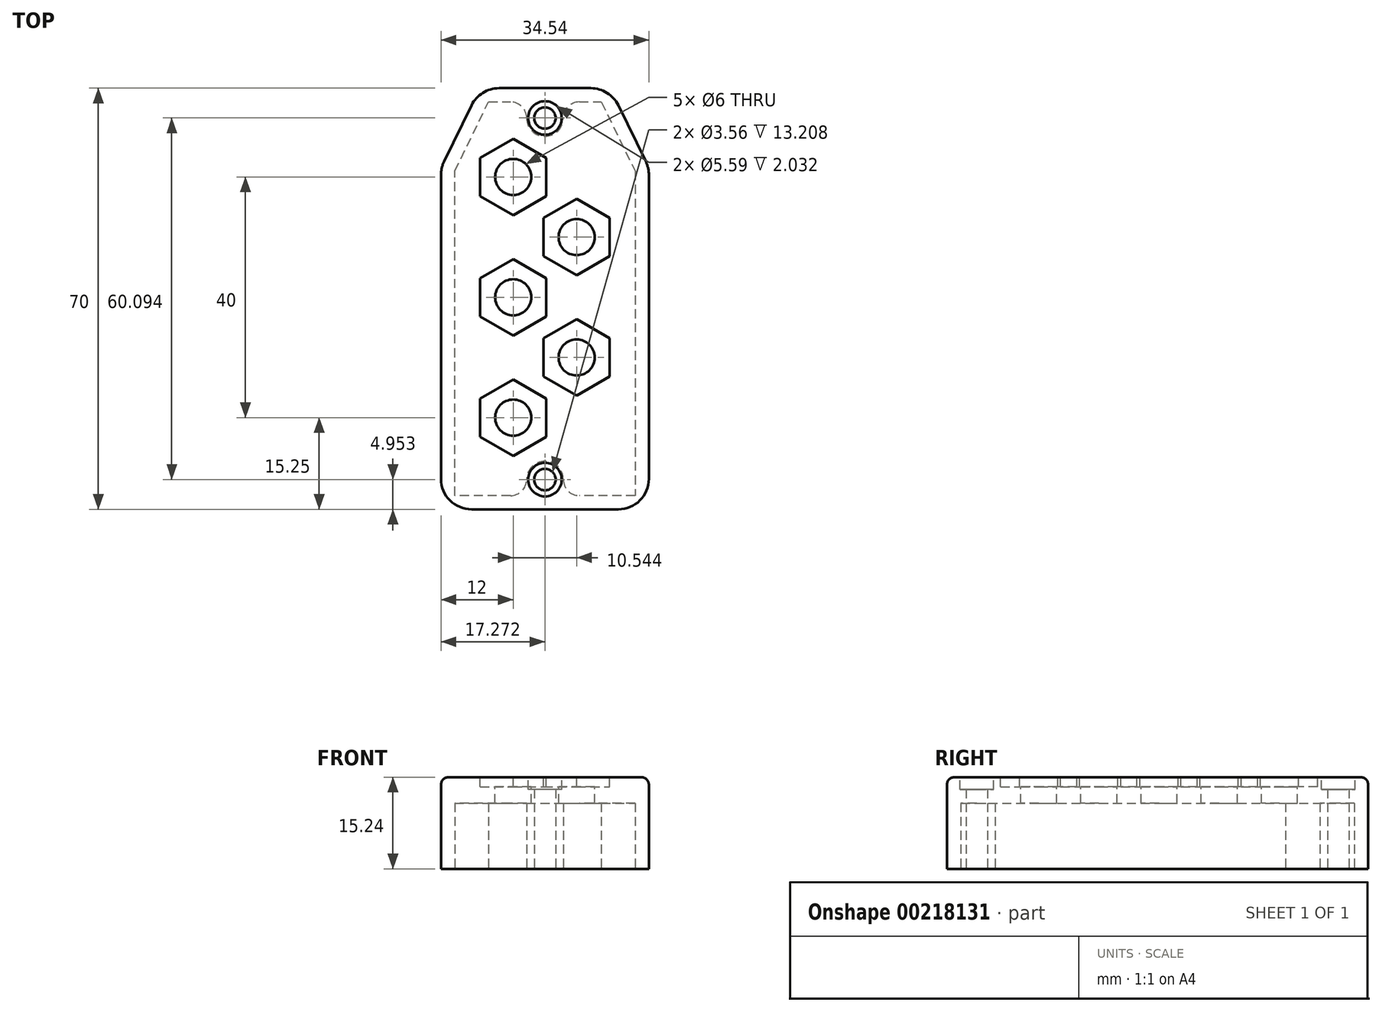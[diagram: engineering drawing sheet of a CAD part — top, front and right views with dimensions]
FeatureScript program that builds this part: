
annotation { "Feature Type Name" : "Feature", "Feature Type Description" : "" }
export const myFeature = defineFeature(function(context is Context, id is Id, definition is map)
    precondition{}
    {
        {
            var Q0;
            Q0=qCreatedBy(makeId("Top.planeOp"),FACE);
            var sketch = newSketch(context, id + "F0", { "sketchPlane" : qUnion([Q0])});
            skLineSegment(sketch, "E0", {"start": v(0, 0) * mm, "end": v(0, 56.78) * mm});
            skLineSegment(sketch, "E1", {"start": v(0, 56.78) * mm, "end": v(6.48, 70) * mm});
            skLineSegment(sketch, "E2", {"start": v(6.48, 70) * mm, "end": v(28.07, 70) * mm});
            skLineSegment(sketch, "E3", {"start": v(28.07, 70) * mm, "end": v(34.54, 56.78) * mm});
            skLineSegment(sketch, "E4", {"start": v(34.54, 56.78) * mm, "end": v(34.54, 0) * mm});
            skLineSegment(sketch, "E5", {"start": v(34.54, 0) * mm, "end": v(0, 0) * mm});
            skLineSegment(sketch, "E6", {"start": v(17.27, 70) * mm, "end": v(17.27, 0) * mm, "construction": true});
            skCircle(sketch, "E7", {"center": v(17.27, 65.05) * mm, "radius": 1.78 * mm});
            skCircle(sketch, "E8", {"center": v(17.27, 4.95) * mm, "radius": 1.78 * mm});
            skSolve(sketch);
        }
        {
            var Q0;
            Q0=makeQuery(id+"F0.imprint","IMPRINT",FACE,{"disambiguationData":[TD([[makeQuery(id+"F0.imprint","IMPRINT",EDGE,{"derivedFrom":sQuery(id+"F0.wireOp",EDGE,"E0")}),-1.0]])]});
            extrude(context, id + "F1", {"entities" : qUnion([Q0]), "depth" : 15.24 * mm});
        }
        {
            var Q0;
            Q0=makeQuery(id+"F1.opExtrude","CAP_FACE",FACE,{"disambiguationData":[OSD([sQuery(id+"F0.wireOp",EDGE,"E0"),sQuery(id+"F0.wireOp",EDGE,"E1"),sQuery(id+"F0.wireOp",EDGE,"E2"),sQuery(id+"F0.wireOp",EDGE,"E3"),sQuery(id+"F0.wireOp",EDGE,"E4"),sQuery(id+"F0.wireOp",EDGE,"E5"),sQuery(id+"F0.wireOp",EDGE,"E7"),sQuery(id+"F0.wireOp",EDGE,"E8")])],"isStart":true});
            var sketch = newSketch(context, id + "F2", { "sketchPlane" : qUnion([Q0])});
            skLineSegment(sketch, "E9.0", {"start": v(32.26, -56.25) * mm, "end": v(32.26, -2.29) * mm});
            skLineSegment(sketch, "E9.1", {"start": v(2.29, -2.29) * mm, "end": v(2.29, -56.25) * mm});
            skLineSegment(sketch, "E9.2", {"start": v(2.29, -56.25) * mm, "end": v(7.9, -67.71) * mm});
            skLineSegment(sketch, "E9.3", {"start": v(32.26, -2.29) * mm, "end": v(22.99, -2.29) * mm});
            skLineSegment(sketch, "E9.4", {"start": v(7.9, -67.71) * mm, "end": v(11.56, -67.71) * mm});
            skLineSegment(sketch, "E9.5", {"start": v(26.64, -67.71) * mm, "end": v(32.26, -56.25) * mm});
            skArc(sketch, "E10.0", {"start": v(14.22, -4.95) * mm, "mid": v(17.27, -8) * mm, "end": v(20.32, -4.95) * mm});
            skArc(sketch, "E11.0", {"start": v(20.32, -65.05) * mm, "mid": v(17.27, -62) * mm, "end": v(14.22, -65.05) * mm});
            skArc(sketch, "E12", {"start": v(14.22, -4.95) * mm, "mid": v(13.44, -3.07) * mm, "end": v(11.56, -2.29) * mm});
            skArc(sketch, "E13", {"start": v(22.99, -2.29) * mm, "mid": v(21.1, -3.07) * mm, "end": v(20.32, -4.95) * mm});
            skArc(sketch, "E14", {"start": v(20.32, -65.05) * mm, "mid": v(21.1, -66.93) * mm, "end": v(22.99, -67.71) * mm});
            skArc(sketch, "E15", {"start": v(11.56, -67.71) * mm, "mid": v(13.44, -66.93) * mm, "end": v(14.22, -65.05) * mm});
            skLineSegment(sketch, "E16.trimOffspring", {"start": v(11.56, -2.29) * mm, "end": v(2.29, -2.29) * mm});
            skPoint(sketch, "E17.start.orphan", {"position": v(14.22, -2.29) * mm});
            skPoint(sketch, "E18.trimOffspring.start.orphan", {"position": v(20.32, -2.29) * mm});
            skLineSegment(sketch, "E19.trimOffspring", {"start": v(22.99, -67.71) * mm, "end": v(26.64, -67.71) * mm});
            skPoint(sketch, "E20.orphan", {"position": v(14.22, -67.71) * mm});
            skPoint(sketch, "E21.orphan", {"position": v(18.75, -67.71) * mm});
            skPoint(sketch, "E22.start.orphan", {"position": v(20.32, -67.71) * mm});
            skSolve(sketch);
        }
        {
            var Q0;
            Q0 = qSketchRegion(id + "F2", true);
            extrude(context, id + "F3", {"entities" : qUnion([Q0]), "operationType" : NewBodyOperationType.REMOVE, "oppositeDirection" : true, "depth" : 10.92 * mm});
        }
        {
            var Q0;
            Q0=makeQuery(id+"F1.opExtrude","SWEPT_EDGE",EDGE,{"disambiguationData":[OSD([sQuery(id+"F0.wireOp",EDGE,"E1"),sQuery(id+"F0.wireOp",EDGE,"E2")])]});
            var Q1;
            Q1=makeQuery(id+"F1.opExtrude","SWEPT_EDGE",EDGE,{"disambiguationData":[OSD([sQuery(id+"F0.wireOp",EDGE,"E2"),sQuery(id+"F0.wireOp",EDGE,"E3")])]});
            var Q2;
            Q2=makeQuery(id+"F1.opExtrude","SWEPT_EDGE",EDGE,{"disambiguationData":[OSD([sQuery(id+"F0.wireOp",EDGE,"E3"),sQuery(id+"F0.wireOp",EDGE,"E4")])]});
            var Q3;
            Q3=makeQuery(id+"F1.opExtrude","SWEPT_EDGE",EDGE,{"disambiguationData":[OSD([sQuery(id+"F0.wireOp",EDGE,"E4"),sQuery(id+"F0.wireOp",EDGE,"E5")])]});
            var Q4;
            Q4=makeQuery(id+"F1.opExtrude","SWEPT_EDGE",EDGE,{"disambiguationData":[OSD([sQuery(id+"F0.wireOp",EDGE,"E0"),sQuery(id+"F0.wireOp",EDGE,"E5")])]});
            var Q5;
            Q5=makeQuery(id+"F1.opExtrude","SWEPT_EDGE",EDGE,{"disambiguationData":[OSD([sQuery(id+"F0.wireOp",EDGE,"E0"),sQuery(id+"F0.wireOp",EDGE,"E1")])]});
            fillet(context, id + "F4", {"entities" : qUnion([Q0, Q1, Q2, Q3, Q4, Q5]), "radius" : 5.08 * mm, "tangentPropagation" : true, "allowEdgeOverflow" : false});
        }
        {
            var Q0;
            {var subQ0=sQuery(id+"F0.wireOp",EDGE,"E5");var subQ1=sQuery(id+"F0.wireOp",EDGE,"E0");Q0=makeQuery(id+"F4.opFillet","BLEND_EDGE",EDGE,{"blendedFrom":[makeQuery(id+"F1.opExtrude","SWEPT_EDGE",EDGE,{"disambiguationData":[OSD([subQ1,subQ0])]}),makeQuery(id+"F1.opExtrude","CAP_FACE",FACE,{"disambiguationData":[OSD([subQ1,sQuery(id+"F0.wireOp",EDGE,"E1"),sQuery(id+"F0.wireOp",EDGE,"E2"),sQuery(id+"F0.wireOp",EDGE,"E3"),sQuery(id+"F0.wireOp",EDGE,"E4"),subQ0,sQuery(id+"F0.wireOp",EDGE,"E7"),sQuery(id+"F0.wireOp",EDGE,"E8")])],"isStart":false})],"blendedInto":[makeQuery(id+"F1.opExtrude","CAP_FACE",FACE,{"disambiguationData":[OSD([subQ1,sQuery(id+"F0.wireOp",EDGE,"E1"),sQuery(id+"F0.wireOp",EDGE,"E2"),sQuery(id+"F0.wireOp",EDGE,"E3"),sQuery(id+"F0.wireOp",EDGE,"E4"),subQ0,sQuery(id+"F0.wireOp",EDGE,"E7"),sQuery(id+"F0.wireOp",EDGE,"E8")])],"isStart":false})]});}
            var Q1;
            {var subQ0=sQuery(id+"F0.wireOp",EDGE,"E5");var subQ1=sQuery(id+"F0.wireOp",EDGE,"E4");Q1=makeQuery(id+"F4.opFillet","BLEND_EDGE",EDGE,{"blendedFrom":[makeQuery(id+"F1.opExtrude","SWEPT_EDGE",EDGE,{"disambiguationData":[OSD([subQ1,subQ0])]}),makeQuery(id+"F1.opExtrude","CAP_FACE",FACE,{"disambiguationData":[OSD([sQuery(id+"F0.wireOp",EDGE,"E0"),sQuery(id+"F0.wireOp",EDGE,"E1"),sQuery(id+"F0.wireOp",EDGE,"E2"),sQuery(id+"F0.wireOp",EDGE,"E3"),subQ1,subQ0,sQuery(id+"F0.wireOp",EDGE,"E7"),sQuery(id+"F0.wireOp",EDGE,"E8")])],"isStart":false})],"blendedInto":[makeQuery(id+"F1.opExtrude","CAP_FACE",FACE,{"disambiguationData":[OSD([sQuery(id+"F0.wireOp",EDGE,"E0"),sQuery(id+"F0.wireOp",EDGE,"E1"),sQuery(id+"F0.wireOp",EDGE,"E2"),sQuery(id+"F0.wireOp",EDGE,"E3"),subQ1,subQ0,sQuery(id+"F0.wireOp",EDGE,"E7"),sQuery(id+"F0.wireOp",EDGE,"E8")])],"isStart":false})]});}
            var Q2;
            {var subQ0=sQuery(id+"F0.wireOp",EDGE,"E4");var subQ1=sQuery(id+"F0.wireOp",EDGE,"E3");Q2=makeQuery(id+"F4.opFillet","BLEND_EDGE",EDGE,{"blendedFrom":[makeQuery(id+"F1.opExtrude","SWEPT_EDGE",EDGE,{"disambiguationData":[OSD([subQ1,subQ0])]}),makeQuery(id+"F1.opExtrude","CAP_FACE",FACE,{"disambiguationData":[OSD([sQuery(id+"F0.wireOp",EDGE,"E0"),sQuery(id+"F0.wireOp",EDGE,"E1"),sQuery(id+"F0.wireOp",EDGE,"E2"),subQ1,subQ0,sQuery(id+"F0.wireOp",EDGE,"E5"),sQuery(id+"F0.wireOp",EDGE,"E7"),sQuery(id+"F0.wireOp",EDGE,"E8")])],"isStart":false})],"blendedInto":[makeQuery(id+"F1.opExtrude","CAP_FACE",FACE,{"disambiguationData":[OSD([sQuery(id+"F0.wireOp",EDGE,"E0"),sQuery(id+"F0.wireOp",EDGE,"E1"),sQuery(id+"F0.wireOp",EDGE,"E2"),subQ1,subQ0,sQuery(id+"F0.wireOp",EDGE,"E5"),sQuery(id+"F0.wireOp",EDGE,"E7"),sQuery(id+"F0.wireOp",EDGE,"E8")])],"isStart":false})]});}
            var Q3;
            {var subQ0=sQuery(id+"F0.wireOp",EDGE,"E1");var subQ1=sQuery(id+"F0.wireOp",EDGE,"E0");Q3=makeQuery(id+"F4.opFillet","BLEND_EDGE",EDGE,{"blendedFrom":[makeQuery(id+"F1.opExtrude","SWEPT_EDGE",EDGE,{"disambiguationData":[OSD([subQ1,subQ0])]}),makeQuery(id+"F1.opExtrude","CAP_FACE",FACE,{"disambiguationData":[OSD([subQ1,subQ0,sQuery(id+"F0.wireOp",EDGE,"E2"),sQuery(id+"F0.wireOp",EDGE,"E3"),sQuery(id+"F0.wireOp",EDGE,"E4"),sQuery(id+"F0.wireOp",EDGE,"E5"),sQuery(id+"F0.wireOp",EDGE,"E7"),sQuery(id+"F0.wireOp",EDGE,"E8")])],"isStart":false})],"blendedInto":[makeQuery(id+"F1.opExtrude","CAP_FACE",FACE,{"disambiguationData":[OSD([subQ1,subQ0,sQuery(id+"F0.wireOp",EDGE,"E2"),sQuery(id+"F0.wireOp",EDGE,"E3"),sQuery(id+"F0.wireOp",EDGE,"E4"),sQuery(id+"F0.wireOp",EDGE,"E5"),sQuery(id+"F0.wireOp",EDGE,"E7"),sQuery(id+"F0.wireOp",EDGE,"E8")])],"isStart":false})]});}
            var Q4;
            {var subQ0=sQuery(id+"F0.wireOp",EDGE,"E3");var subQ1=sQuery(id+"F0.wireOp",EDGE,"E2");Q4=makeQuery(id+"F4.opFillet","BLEND_EDGE",EDGE,{"blendedFrom":[makeQuery(id+"F1.opExtrude","SWEPT_EDGE",EDGE,{"disambiguationData":[OSD([subQ1,subQ0])]}),makeQuery(id+"F1.opExtrude","CAP_FACE",FACE,{"disambiguationData":[OSD([sQuery(id+"F0.wireOp",EDGE,"E0"),sQuery(id+"F0.wireOp",EDGE,"E1"),subQ1,subQ0,sQuery(id+"F0.wireOp",EDGE,"E4"),sQuery(id+"F0.wireOp",EDGE,"E5"),sQuery(id+"F0.wireOp",EDGE,"E7"),sQuery(id+"F0.wireOp",EDGE,"E8")])],"isStart":false})],"blendedInto":[makeQuery(id+"F1.opExtrude","CAP_FACE",FACE,{"disambiguationData":[OSD([sQuery(id+"F0.wireOp",EDGE,"E0"),sQuery(id+"F0.wireOp",EDGE,"E1"),subQ1,subQ0,sQuery(id+"F0.wireOp",EDGE,"E4"),sQuery(id+"F0.wireOp",EDGE,"E5"),sQuery(id+"F0.wireOp",EDGE,"E7"),sQuery(id+"F0.wireOp",EDGE,"E8")])],"isStart":false})]});}
            var Q5;
            {var subQ0=sQuery(id+"F0.wireOp",EDGE,"E2");var subQ1=sQuery(id+"F0.wireOp",EDGE,"E1");Q5=makeQuery(id+"F4.opFillet","BLEND_EDGE",EDGE,{"blendedFrom":[makeQuery(id+"F1.opExtrude","SWEPT_EDGE",EDGE,{"disambiguationData":[OSD([subQ1,subQ0])]}),makeQuery(id+"F1.opExtrude","CAP_FACE",FACE,{"disambiguationData":[OSD([sQuery(id+"F0.wireOp",EDGE,"E0"),subQ1,subQ0,sQuery(id+"F0.wireOp",EDGE,"E3"),sQuery(id+"F0.wireOp",EDGE,"E4"),sQuery(id+"F0.wireOp",EDGE,"E5"),sQuery(id+"F0.wireOp",EDGE,"E7"),sQuery(id+"F0.wireOp",EDGE,"E8")])],"isStart":false})],"blendedInto":[makeQuery(id+"F1.opExtrude","CAP_FACE",FACE,{"disambiguationData":[OSD([sQuery(id+"F0.wireOp",EDGE,"E0"),subQ1,subQ0,sQuery(id+"F0.wireOp",EDGE,"E3"),sQuery(id+"F0.wireOp",EDGE,"E4"),sQuery(id+"F0.wireOp",EDGE,"E5"),sQuery(id+"F0.wireOp",EDGE,"E7"),sQuery(id+"F0.wireOp",EDGE,"E8")])],"isStart":false})]});}
            var Q6;
            Q6=makeQuery(id+"F1.opExtrude","CAP_EDGE",EDGE,{"disambiguationData":[OSD([sQuery(id+"F0.wireOp",EDGE,"E5")])],"isStart":false});
            var Q7;
            Q7=makeQuery(id+"F1.opExtrude","CAP_EDGE",EDGE,{"disambiguationData":[OSD([sQuery(id+"F0.wireOp",EDGE,"E0")])],"isStart":false});
            var Q8;
            Q8=makeQuery(id+"F1.opExtrude","CAP_EDGE",EDGE,{"disambiguationData":[OSD([sQuery(id+"F0.wireOp",EDGE,"E1")])],"isStart":false});
            var Q9;
            Q9=makeQuery(id+"F1.opExtrude","CAP_EDGE",EDGE,{"disambiguationData":[OSD([sQuery(id+"F0.wireOp",EDGE,"E2")])],"isStart":false});
            var Q10;
            Q10=makeQuery(id+"F1.opExtrude","CAP_EDGE",EDGE,{"disambiguationData":[OSD([sQuery(id+"F0.wireOp",EDGE,"E3")])],"isStart":false});
            var Q11;
            Q11=makeQuery(id+"F1.opExtrude","CAP_EDGE",EDGE,{"disambiguationData":[OSD([sQuery(id+"F0.wireOp",EDGE,"E4")])],"isStart":false});
            fillet(context, id + "F5", {"entities" : qUnion([Q0, Q1, Q2, Q3, Q4, Q5, Q6, Q7, Q8, Q9, Q10, Q11]), "radius" : 1.27 * mm, "tangentPropagation" : true, "allowEdgeOverflow" : false});
        }
        {
            var Q0;
            Q0=makeQuery(id+"F1.opExtrude","CAP_FACE",FACE,{"disambiguationData":[OSD([sQuery(id+"F0.wireOp",EDGE,"E0"),sQuery(id+"F0.wireOp",EDGE,"E1"),sQuery(id+"F0.wireOp",EDGE,"E2"),sQuery(id+"F0.wireOp",EDGE,"E3"),sQuery(id+"F0.wireOp",EDGE,"E4"),sQuery(id+"F0.wireOp",EDGE,"E5"),sQuery(id+"F0.wireOp",EDGE,"E7"),sQuery(id+"F0.wireOp",EDGE,"E8")])],"isStart":false});
            var sketch = newSketch(context, id + "F6", { "sketchPlane" : qUnion([Q0])});
            skCircle(sketch, "E23", {"center": v(17.27, 65.05) * mm, "radius": 2.8 * mm});
            skCircle(sketch, "E24", {"center": v(17.27, 4.95) * mm, "radius": 2.8 * mm});
            skSolve(sketch);
        }
        {
            var Q0;
            Q0 = qSketchRegion(id + "F6", true);
            extrude(context, id + "F7", {"entities" : qUnion([Q0]), "operationType" : NewBodyOperationType.REMOVE, "oppositeDirection" : true, "depth" : 2.03 * mm});
        }
        {
            var Q0;
            Q0=makeQuery(id+"F1.opExtrude","CAP_FACE",FACE,{"disambiguationData":[OSD([sQuery(id+"F0.wireOp",EDGE,"E0"),sQuery(id+"F0.wireOp",EDGE,"E1"),sQuery(id+"F0.wireOp",EDGE,"E2"),sQuery(id+"F0.wireOp",EDGE,"E3"),sQuery(id+"F0.wireOp",EDGE,"E4"),sQuery(id+"F0.wireOp",EDGE,"E5"),sQuery(id+"F0.wireOp",EDGE,"E7"),sQuery(id+"F0.wireOp",EDGE,"E8")])],"isStart":false});
            var sketch = newSketch(context, id + "F8", { "sketchPlane" : qUnion([Q0])});
            skLineSegment(sketch, "E25.0", {"start": v(6.5, 52.07) * mm, "end": v(6.5, 58.43) * mm});
            skLineSegment(sketch, "E25.1", {"start": v(6.5, 58.43) * mm, "end": v(12, 61.6) * mm});
            skLineSegment(sketch, "E25.2", {"start": v(12, 61.6) * mm, "end": v(17.5, 58.43) * mm});
            skLineSegment(sketch, "E25.3", {"start": v(17.5, 58.43) * mm, "end": v(17.5, 52.07) * mm});
            skLineSegment(sketch, "E25.4", {"start": v(17.5, 52.07) * mm, "end": v(12, 48.9) * mm});
            skLineSegment(sketch, "E25.5", {"start": v(12, 48.9) * mm, "end": v(6.5, 52.07) * mm});
            skPoint(sketch, "E25.0.midPoint", {"position": v(6.5, 55.25) * mm});
            skLineSegment(sketch, "E26.1.0.0", {"start": v(12, 41.6) * mm, "end": v(17.5, 38.43) * mm});
            skLineSegment(sketch, "E26.1.0.1", {"start": v(12, 28.9) * mm, "end": v(6.5, 32.07) * mm});
            skPoint(sketch, "E26.1.0.2", {"position": v(6.5, 35.25) * mm});
            skLineSegment(sketch, "E26.1.0.3", {"start": v(17.5, 38.43) * mm, "end": v(17.5, 32.07) * mm});
            skLineSegment(sketch, "E26.1.0.4", {"start": v(6.5, 38.43) * mm, "end": v(12, 41.6) * mm});
            skLineSegment(sketch, "E26.1.0.5", {"start": v(17.5, 32.07) * mm, "end": v(12, 28.9) * mm});
            skLineSegment(sketch, "E26.1.0.6", {"start": v(6.5, 32.07) * mm, "end": v(6.5, 38.43) * mm});
            skLineSegment(sketch, "E26.2.0.0", {"start": v(12, 21.6) * mm, "end": v(17.5, 18.43) * mm});
            skLineSegment(sketch, "E26.2.0.1", {"start": v(12, 8.9) * mm, "end": v(6.5, 12.07) * mm});
            skPoint(sketch, "E26.2.0.2", {"position": v(6.5, 15.25) * mm});
            skLineSegment(sketch, "E26.2.0.3", {"start": v(17.5, 18.43) * mm, "end": v(17.5, 12.07) * mm});
            skLineSegment(sketch, "E26.2.0.4", {"start": v(6.5, 18.43) * mm, "end": v(12, 21.6) * mm});
            skLineSegment(sketch, "E26.2.0.5", {"start": v(17.5, 12.07) * mm, "end": v(12, 8.9) * mm});
            skLineSegment(sketch, "E26.2.0.6", {"start": v(6.5, 12.07) * mm, "end": v(6.5, 18.43) * mm});
            skLineSegment(sketch, "E27.0", {"start": v(28.04, 48.43) * mm, "end": v(28.04, 42.07) * mm});
            skLineSegment(sketch, "E27.1", {"start": v(28.04, 42.07) * mm, "end": v(22.54, 38.9) * mm});
            skLineSegment(sketch, "E27.2", {"start": v(22.54, 38.9) * mm, "end": v(17.04, 42.07) * mm});
            skLineSegment(sketch, "E27.3", {"start": v(17.04, 42.07) * mm, "end": v(17.04, 48.43) * mm});
            skLineSegment(sketch, "E27.4", {"start": v(17.04, 48.43) * mm, "end": v(22.54, 51.6) * mm});
            skLineSegment(sketch, "E27.5", {"start": v(22.54, 51.6) * mm, "end": v(28.04, 48.43) * mm});
            skPoint(sketch, "E27.0.midPoint", {"position": v(28.04, 45.25) * mm});
            skLineSegment(sketch, "E28.0", {"start": v(28.04, 28.43) * mm, "end": v(28.04, 22.07) * mm});
            skLineSegment(sketch, "E28.1", {"start": v(28.04, 22.07) * mm, "end": v(22.54, 18.9) * mm});
            skLineSegment(sketch, "E28.2", {"start": v(22.54, 18.9) * mm, "end": v(17.04, 22.07) * mm});
            skLineSegment(sketch, "E28.3", {"start": v(17.04, 22.07) * mm, "end": v(17.04, 28.43) * mm});
            skLineSegment(sketch, "E28.4", {"start": v(17.04, 28.43) * mm, "end": v(22.54, 31.6) * mm});
            skLineSegment(sketch, "E28.5", {"start": v(22.54, 31.6) * mm, "end": v(28.04, 28.43) * mm});
            skPoint(sketch, "E28.0.midPoint", {"position": v(28.04, 25.25) * mm});
            skSolve(sketch);
        }
        {
            var Q0;
            Q0=makeQuery(id+"F8.imprint","IMPRINT",FACE,{"disambiguationData":[TD([[makeQuery(id+"F8.imprint","IMPRINT",EDGE,{"derivedFrom":sQuery(id+"F8.wireOp",EDGE,"E26.2.0.0")}),-1.0]])]});
            var Q1;
            Q1=makeQuery(id+"F8.imprint","IMPRINT",FACE,{"disambiguationData":[TD([[makeQuery(id+"F8.imprint","IMPRINT",EDGE,{"derivedFrom":sQuery(id+"F8.wireOp",EDGE,"E26.1.0.0")}),-1.0]])]});
            var Q2;
            Q2=makeQuery(id+"F8.imprint","IMPRINT",FACE,{"disambiguationData":[TD([[makeQuery(id+"F8.imprint","IMPRINT",EDGE,{"derivedFrom":sQuery(id+"F8.wireOp",EDGE,"E27.0")}),-1.0]])]});
            var Q3;
            Q3=makeQuery(id+"F8.imprint","IMPRINT",FACE,{"disambiguationData":[TD([[makeQuery(id+"F8.imprint","IMPRINT",EDGE,{"derivedFrom":sQuery(id+"F8.wireOp",EDGE,"E25.0")}),-1.0]])]});
            var Q4;
            Q4=makeQuery(id+"F8.imprint","IMPRINT",FACE,{"disambiguationData":[TD([[makeQuery(id+"F8.imprint","IMPRINT",EDGE,{"derivedFrom":sQuery(id+"F8.wireOp",EDGE,"E28.0")}),-1.0]])]});
            extrude(context, id + "F9", {"entities" : qUnion([Q0, Q1, Q2, Q3, Q4]), "operationType" : NewBodyOperationType.REMOVE, "oppositeDirection" : true, "depth" : 1.6 * mm});
        }
        {
            var Q0;
            Q0=makeQuery(id+"F9.boolean.opBoolean","COPY",FACE,{"derivedFrom":makeQuery(id+"F9.opExtrude","CAP_FACE",FACE,{"disambiguationData":[OSD([sQuery(id+"F8.wireOp",EDGE,"E26.1.0.0"),sQuery(id+"F8.wireOp",EDGE,"E26.1.0.1"),sQuery(id+"F8.wireOp",EDGE,"E26.1.0.3"),sQuery(id+"F8.wireOp",EDGE,"E26.1.0.4"),sQuery(id+"F8.wireOp",EDGE,"E26.1.0.5"),sQuery(id+"F8.wireOp",EDGE,"E26.1.0.6")])],"isStart":false})});
            var sketch = newSketch(context, id + "F10", { "sketchPlane" : qUnion([Q0])});
            skCircle(sketch, "E29", {"center": v(12, 35.25) * mm, "radius": 3 * mm});
            skPoint(sketch, "E29.centerSnap0", {"position": v(17.5, 35.25) * mm});
            skSolve(sketch);
        }
        {
            var Q0;
            Q0=makeQuery(id+"F10.imprint","IMPRINT",FACE,{"disambiguationData":[TD([[makeQuery(id+"F10.imprint","IMPRINT",EDGE,{"derivedFrom":sQuery(id+"F10.wireOp",EDGE,"E29")}),1.0]])]});
            extrude(context, id + "F11", {"entities" : qUnion([Q0]), "operationType" : NewBodyOperationType.REMOVE, "oppositeDirection" : true, "depth" : 25 * mm});
        }
        {
            var Q0;
            Q0=makeQuery(id+"F9.boolean.opBoolean","COPY",FACE,{"derivedFrom":makeQuery(id+"F9.opExtrude","CAP_FACE",FACE,{"disambiguationData":[OSD([sQuery(id+"F8.wireOp",EDGE,"E27.0"),sQuery(id+"F8.wireOp",EDGE,"E27.1"),sQuery(id+"F8.wireOp",EDGE,"E27.2"),sQuery(id+"F8.wireOp",EDGE,"E27.3"),sQuery(id+"F8.wireOp",EDGE,"E27.4"),sQuery(id+"F8.wireOp",EDGE,"E27.5")])],"isStart":false})});
            var sketch = newSketch(context, id + "F12", { "sketchPlane" : qUnion([Q0])});
            skCircle(sketch, "E30", {"center": v(22.54, 45.25) * mm, "radius": 3 * mm});
            skPoint(sketch, "E30.centerSnap0", {"position": v(17.04, 45.25) * mm});
            skSolve(sketch);
        }
        {
            var Q0;
            Q0=makeQuery(id+"F12.imprint","IMPRINT",FACE,{"disambiguationData":[TD([[makeQuery(id+"F12.imprint","IMPRINT",EDGE,{"derivedFrom":sQuery(id+"F12.wireOp",EDGE,"E30")}),1.0]])]});
            var Q1;
            Q1=sQuery(id+"F12.wireOp",EDGE,"E30");
            extrude(context, id + "F13", {"entities" : qUnion([Q0]), "operationType" : NewBodyOperationType.REMOVE, "surfaceEntities" : qUnion([Q1]), "oppositeDirection" : true, "depth" : 25 * mm});
        }
        {
            var Q0;
            Q0=makeQuery(id+"F9.boolean.opBoolean","COPY",FACE,{"derivedFrom":makeQuery(id+"F9.opExtrude","CAP_FACE",FACE,{"disambiguationData":[OSD([sQuery(id+"F8.wireOp",EDGE,"E28.0"),sQuery(id+"F8.wireOp",EDGE,"E28.1"),sQuery(id+"F8.wireOp",EDGE,"E28.2"),sQuery(id+"F8.wireOp",EDGE,"E28.3"),sQuery(id+"F8.wireOp",EDGE,"E28.4"),sQuery(id+"F8.wireOp",EDGE,"E28.5")])],"isStart":false})});
            var sketch = newSketch(context, id + "F14", { "sketchPlane" : qUnion([Q0])});
            skCircle(sketch, "E31", {"center": v(22.54, 25.25) * mm, "radius": 3 * mm});
            skPoint(sketch, "E31.centerSnap0", {"position": v(17.04, 25.25) * mm});
            skSolve(sketch);
        }
        {
            var Q0;
            Q0=makeQuery(id+"F14.imprint","IMPRINT",FACE,{"disambiguationData":[TD([[makeQuery(id+"F14.imprint","IMPRINT",EDGE,{"derivedFrom":sQuery(id+"F14.wireOp",EDGE,"E31")}),1.0]])]});
            extrude(context, id + "F15", {"entities" : qUnion([Q0]), "operationType" : NewBodyOperationType.REMOVE, "oppositeDirection" : true, "depth" : 25 * mm});
        }
        {
            var Q0;
            Q0=makeQuery(id+"F9.boolean.opBoolean","COPY",FACE,{"derivedFrom":makeQuery(id+"F9.opExtrude","CAP_FACE",FACE,{"disambiguationData":[OSD([sQuery(id+"F8.wireOp",EDGE,"E26.2.0.0"),sQuery(id+"F8.wireOp",EDGE,"E26.2.0.1"),sQuery(id+"F8.wireOp",EDGE,"E26.2.0.3"),sQuery(id+"F8.wireOp",EDGE,"E26.2.0.4"),sQuery(id+"F8.wireOp",EDGE,"E26.2.0.5"),sQuery(id+"F8.wireOp",EDGE,"E26.2.0.6")])],"isStart":false})});
            var sketch = newSketch(context, id + "F16", { "sketchPlane" : qUnion([Q0])});
            skCircle(sketch, "E32", {"center": v(12, 15.25) * mm, "radius": 3 * mm});
            skPoint(sketch, "E32.centerSnap0", {"position": v(17.5, 15.25) * mm});
            skSolve(sketch);
        }
        {
            var Q0;
            Q0=makeQuery(id+"F16.imprint","IMPRINT",FACE,{"disambiguationData":[TD([[makeQuery(id+"F16.imprint","IMPRINT",EDGE,{"derivedFrom":sQuery(id+"F16.wireOp",EDGE,"E32")}),1.0]])]});
            extrude(context, id + "F17", {"entities" : qUnion([Q0]), "operationType" : NewBodyOperationType.REMOVE, "oppositeDirection" : true, "depth" : 25 * mm});
        }
        {
            var Q0;
            Q0=makeQuery(id+"F9.boolean.opBoolean","COPY",FACE,{"derivedFrom":makeQuery(id+"F9.opExtrude","CAP_FACE",FACE,{"disambiguationData":[OSD([sQuery(id+"F8.wireOp",EDGE,"E25.0"),sQuery(id+"F8.wireOp",EDGE,"E25.1"),sQuery(id+"F8.wireOp",EDGE,"E25.2"),sQuery(id+"F8.wireOp",EDGE,"E25.3"),sQuery(id+"F8.wireOp",EDGE,"E25.4"),sQuery(id+"F8.wireOp",EDGE,"E25.5")])],"isStart":false})});
            var sketch = newSketch(context, id + "F18", { "sketchPlane" : qUnion([Q0])});
            skCircle(sketch, "E33", {"center": v(12, 55.25) * mm, "radius": 3 * mm});
            skPoint(sketch, "E33.centerSnap0", {"position": v(17.5, 55.25) * mm});
            skArc(sketch, "E34.0.0", {"start": v(9.65, 68.73) * mm, "mid": v(7.63, 68.15) * mm, "end": v(6.22, 66.6) * mm});
            skLineSegment(sketch, "E34.0.1", {"start": v(6.22, 66.6) * mm, "end": v(1.66, 57.27) * mm});
            skArc(sketch, "E34.0.2", {"start": v(1.66, 57.27) * mm, "mid": v(1.37, 56.46) * mm, "end": v(1.27, 55.6) * mm});
            skLineSegment(sketch, "E34.0.3", {"start": v(1.27, 55.6) * mm, "end": v(1.27, 5.08) * mm});
            skArc(sketch, "E34.0.4", {"start": v(1.27, 5.08) * mm, "mid": v(2.39, 2.39) * mm, "end": v(5.08, 1.27) * mm});
            skLineSegment(sketch, "E34.0.5", {"start": v(5.08, 1.27) * mm, "end": v(29.46, 1.27) * mm});
            skArc(sketch, "E34.0.6", {"start": v(29.46, 1.27) * mm, "mid": v(32.16, 2.39) * mm, "end": v(33.27, 5.08) * mm});
            skLineSegment(sketch, "E34.0.7", {"start": v(33.27, 5.08) * mm, "end": v(33.27, 55.6) * mm});
            skArc(sketch, "E34.0.8", {"start": v(33.27, 55.6) * mm, "mid": v(33.18, 56.46) * mm, "end": v(32.89, 57.27) * mm});
            skLineSegment(sketch, "E34.0.9", {"start": v(32.89, 57.27) * mm, "end": v(28.32, 66.6) * mm});
            skArc(sketch, "E34.0.10", {"start": v(28.32, 66.6) * mm, "mid": v(26.91, 68.15) * mm, "end": v(24.9, 68.73) * mm});
            skLineSegment(sketch, "E34.0.11", {"start": v(24.9, 68.73) * mm, "end": v(9.65, 68.73) * mm});
            skSolve(sketch);
        }
        {
            var Q0;
            Q0=makeQuery(id+"F18.imprint","IMPRINT",FACE,{"disambiguationData":[TD([[makeQuery(id+"F18.imprint","IMPRINT",EDGE,{"derivedFrom":sQuery(id+"F18.wireOp",EDGE,"E33")}),1.0]])]});
            extrude(context, id + "F19", {"entities" : qUnion([Q0]), "operationType" : NewBodyOperationType.REMOVE, "oppositeDirection" : true, "depth" : 25 * mm});
        }
    });
